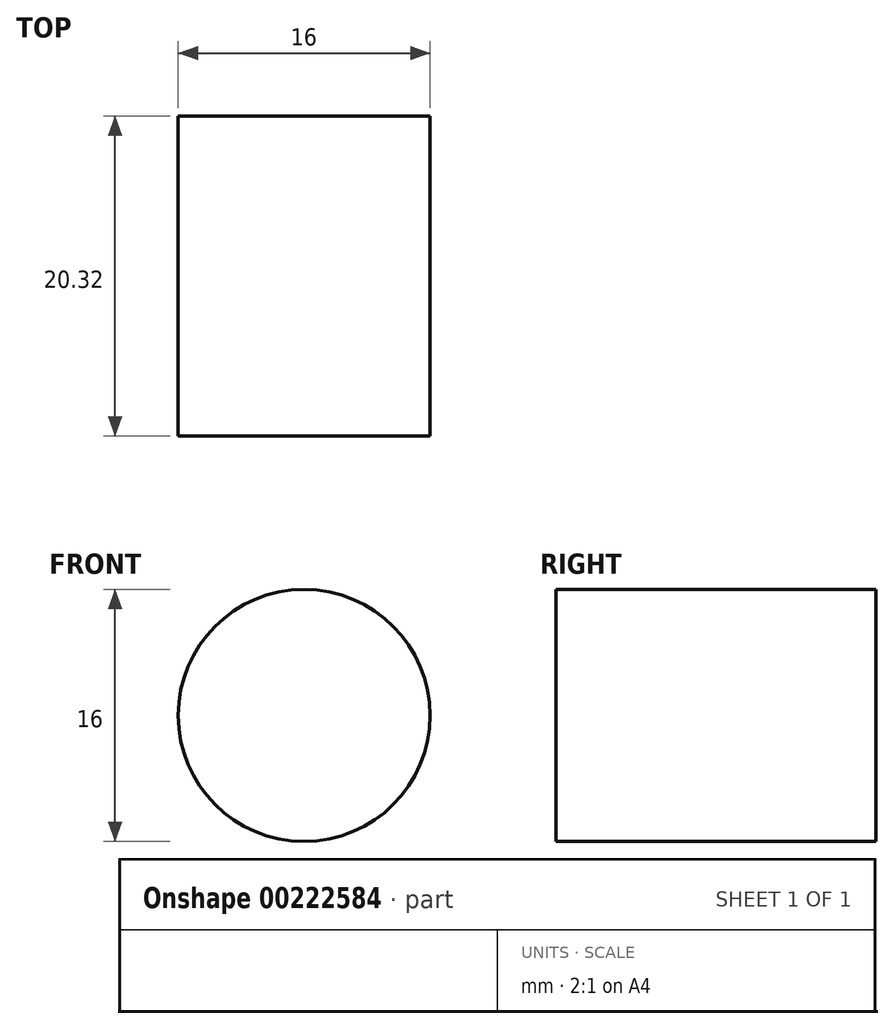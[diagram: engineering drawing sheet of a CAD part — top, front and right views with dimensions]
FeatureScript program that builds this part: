
annotation { "Feature Type Name" : "Feature", "Feature Type Description" : "" }
export const myFeature = defineFeature(function(context is Context, id is Id, definition is map)
    precondition{}
    {
        {
            var Q0;
            Q0=qCreatedBy(makeId("Front.planeOp"),FACE);
            var sketch = newSketch(context, id + "F0", { "sketchPlane" : qUnion([Q0])});
            skCircle(sketch, "E0", {"center": v(0, 0) * mm, "radius": 8 * mm});
            skSolve(sketch);
        }
        {
            var Q0;
            Q0=makeQuery(id+"F0.imprint","IMPRINT",FACE,{"disambiguationData":[TD([[makeQuery(id+"F0.imprint","IMPRINT",EDGE,{"derivedFrom":sQuery(id+"F0.wireOp",EDGE,"E0")}),1.0]])]});
            extrude(context, id + "F1", {"entities" : qUnion([Q0]), "oppositeDirection" : true, "depth" : 20.32 * mm});
        }
    });
